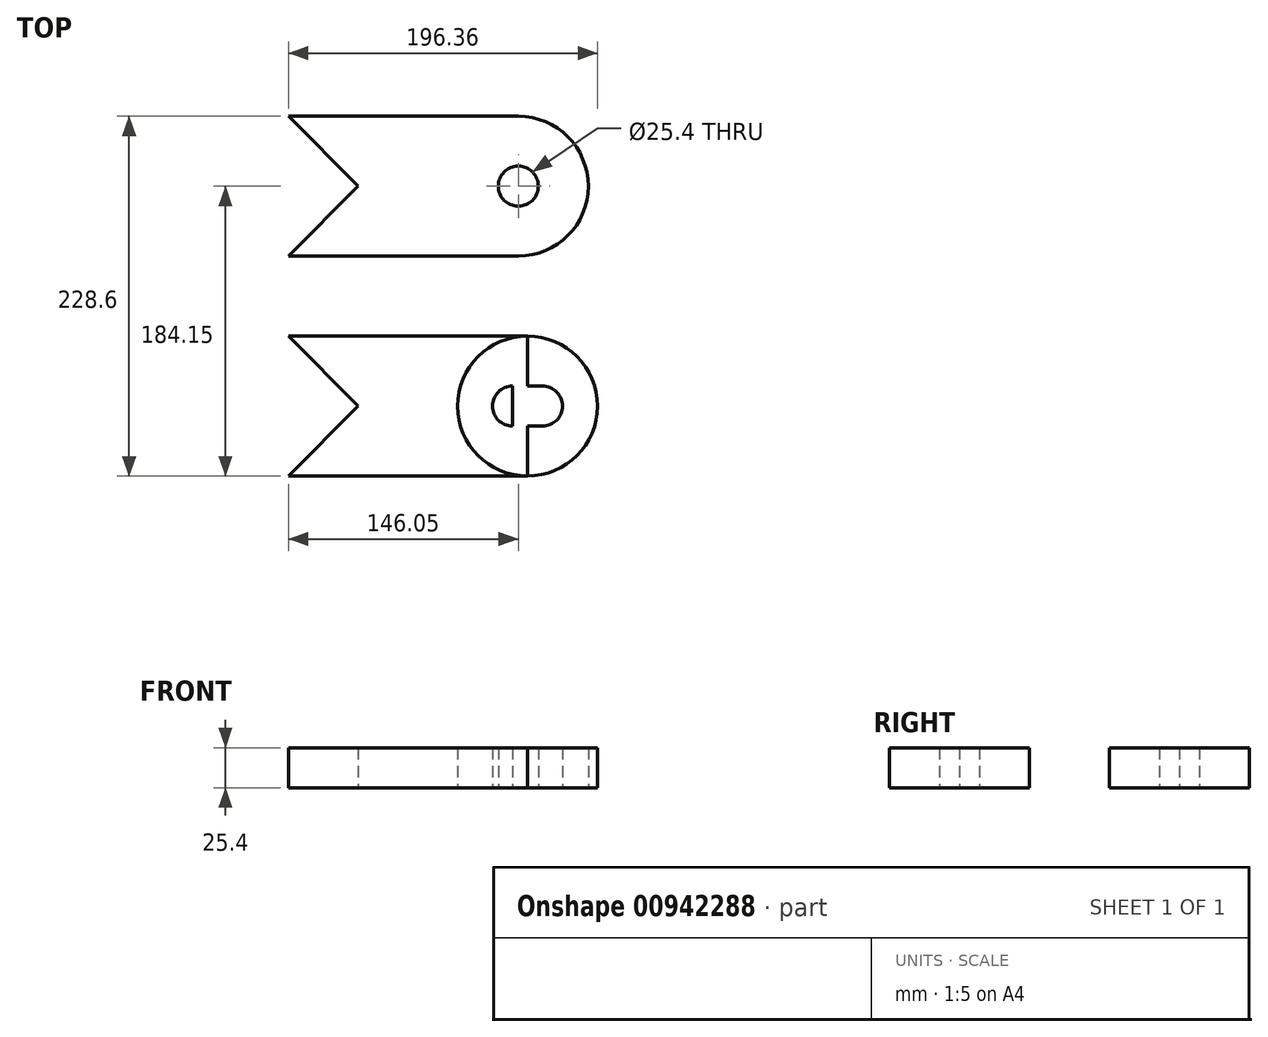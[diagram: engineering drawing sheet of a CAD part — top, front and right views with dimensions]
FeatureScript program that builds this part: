
annotation { "Feature Type Name" : "Feature", "Feature Type Description" : "" }
export const myFeature = defineFeature(function(context is Context, id is Id, definition is map)
    precondition{}
    {
        {
            var Q0;
            Q0=qCreatedBy(makeId("Top.planeOp"),FACE);
            var sketch = newSketch(context, id + "F0", { "sketchPlane" : qUnion([Q0])});
            skLineSegment(sketch, "E0.bottom", {"start": v(0, 0) * mm, "end": v(101.6, 0) * mm});
            skLineSegment(sketch, "E0.top", {"start": v(0, 88.9) * mm, "end": v(101.6, 88.9) * mm});
            skLineSegment(sketch, "E0.left", {"start": v(0, 0) * mm, "end": v(0, 88.9) * mm});
            skLineSegment(sketch, "E0.right", {"start": v(101.6, 0) * mm, "end": v(101.6, 88.9) * mm});
            skCircle(sketch, "E1", {"center": v(101.6, 44.45) * mm, "radius": 44.45 * mm});
            skLineSegment(sketch, "E2", {"start": v(0, 44.45) * mm, "end": v(-44.45, 88.9) * mm});
            skLineSegment(sketch, "E3", {"start": v(0, 44.45) * mm, "end": v(-44.45, 0) * mm});
            skLineSegment(sketch, "E4", {"start": v(0, 0) * mm, "end": v(-44.45, 0) * mm});
            skLineSegment(sketch, "E5", {"start": v(0, 88.9) * mm, "end": v(-44.45, 88.9) * mm});
            skCircle(sketch, "E6", {"center": v(101.6, 44.45) * mm, "radius": 12.7 * mm});
            skLineSegment(sketch, "E7.bottom", {"start": v(0, -50.8) * mm, "end": v(107.46, -50.8) * mm});
            skLineSegment(sketch, "E7.top", {"start": v(0, -139.7) * mm, "end": v(107.46, -139.7) * mm});
            skLineSegment(sketch, "E7.left", {"start": v(0, -50.8) * mm, "end": v(0, -139.7) * mm});
            skLineSegment(sketch, "E7.right", {"start": v(107.46, -50.8) * mm, "end": v(107.46, -139.7) * mm});
            skCircle(sketch, "E8", {"center": v(107.46, -95.25) * mm, "radius": 44.45 * mm});
            skLineSegment(sketch, "E9", {"start": v(-44.45, 0) * mm, "end": v(-44.45, -150.03) * mm});
            skLineSegment(sketch, "E10", {"start": v(0, -95.25) * mm, "end": v(-44.45, -50.8) * mm});
            skLineSegment(sketch, "E11", {"start": v(-44.45, -50.8) * mm, "end": v(0, -50.8) * mm});
            skLineSegment(sketch, "E12", {"start": v(0, -95.25) * mm, "end": v(-44.45, -139.7) * mm});
            skLineSegment(sketch, "E13", {"start": v(-44.45, -139.7) * mm, "end": v(0, -139.7) * mm});
            skArc(sketch, "E14", {"start": v(116.99, -107.95) * mm, "mid": v(129.69, -95.25) * mm, "end": v(116.99, -82.55) * mm});
            skArc(sketch, "E15.MirrorC", {"start": v(97.94, -107.95) * mm, "mid": v(85.24, -95.25) * mm, "end": v(97.94, -82.55) * mm});
            skLineSegment(sketch, "E16", {"start": v(97.94, -95.25) * mm, "end": v(97.94, -82.55) * mm});
            skLineSegment(sketch, "E17", {"start": v(97.94, -82.55) * mm, "end": v(116.99, -82.55) * mm});
            skLineSegment(sketch, "E18", {"start": v(97.94, -95.25) * mm, "end": v(97.94, -107.95) * mm});
            skLineSegment(sketch, "E19", {"start": v(97.94, -107.95) * mm, "end": v(116.99, -107.95) * mm});
            skSolve(sketch);
        }
        {
            var Q0;
            {var subQ2=sQuery(id+"F0.wireOp",EDGE,"E2");Q0=makeQuery(id+"F0.imprint","IMPRINT",FACE,{"disambiguationData":[TD([[makeQuery(id+"F0.imprint","IMPRINT",EDGE,{"derivedFrom":subQ2}),-1.0]])]});}
            var Q1;
            {var subQ2=sQuery(id+"F0.wireOp",EDGE,"E3");Q1=makeQuery(id+"F0.imprint","IMPRINT",FACE,{"disambiguationData":[TD([[makeQuery(id+"F0.imprint","IMPRINT",EDGE,{"derivedFrom":subQ2}),1.0]])]});}
            var Q2;
            {var subQ3=sQuery(id+"F0.wireOp",EDGE,"E0.bottom");Q2=makeQuery(id+"F0.imprint","IMPRINT",FACE,{"disambiguationData":[TD([[makeQuery(id+"F0.imprint","IMPRINT",EDGE,{"derivedFrom":subQ3}),1.0]])]});}
            var Q3;
            {var subQ1=sQuery(id+"F0.wireOp",EDGE,"E0.right");var subQ3=sQuery(id+"F0.wireOp",EDGE,"E6");var subQ4=makeQuery(id+"F0.imprint","INTERSECT",VERTEX,{"disambiguationData":[OD(0.0)],"derivedFrom":[subQ1,subQ3]});Q3=makeQuery(id+"F0.imprint","IMPRINT",FACE,{"disambiguationData":[TD([[makeQuery(id+"F0.imprint","IMPRINT",EDGE,{"disambiguationData":[TD([[subQ4,1.0]])],"derivedFrom":subQ3}),-1.0]])]});}
            var Q4;
            {var subQ1=sQuery(id+"F0.wireOp",EDGE,"E0.right");var subQ3=sQuery(id+"F0.wireOp",EDGE,"E6");var subQ4=makeQuery(id+"F0.imprint","INTERSECT",VERTEX,{"disambiguationData":[OD(0.0)],"derivedFrom":[subQ1,subQ3]});Q4=makeQuery(id+"F0.imprint","IMPRINT",FACE,{"disambiguationData":[TD([[makeQuery(id+"F0.imprint","IMPRINT",EDGE,{"disambiguationData":[TD([[subQ4,-1.0]])],"derivedFrom":subQ3}),-1.0]])]});}
            var Q5;
            {var subQ2=sQuery(id+"F0.wireOp",EDGE,"E10");Q5=makeQuery(id+"F0.imprint","IMPRINT",FACE,{"disambiguationData":[TD([[makeQuery(id+"F0.imprint","IMPRINT",EDGE,{"derivedFrom":subQ2}),-1.0]])]});}
            var Q6;
            {var subQ2=sQuery(id+"F0.wireOp",EDGE,"E12");Q6=makeQuery(id+"F0.imprint","IMPRINT",FACE,{"disambiguationData":[TD([[makeQuery(id+"F0.imprint","IMPRINT",EDGE,{"derivedFrom":subQ2}),1.0]])]});}
            var Q7;
            {var subQ3=sQuery(id+"F0.wireOp",EDGE,"E7.bottom");Q7=makeQuery(id+"F0.imprint","IMPRINT",FACE,{"disambiguationData":[TD([[makeQuery(id+"F0.imprint","IMPRINT",EDGE,{"derivedFrom":subQ3}),-1.0]])]});}
            var Q8;
            {var subQ0=sQuery(id+"F0.wireOp",EDGE,"E15.MirrorC");Q8=makeQuery(id+"F0.imprint","IMPRINT",FACE,{"disambiguationData":[TD([[makeQuery(id+"F0.imprint","IMPRINT",EDGE,{"derivedFrom":subQ0}),1.0]])]});}
            var Q9;
            {var subQ6=sQuery(id+"F0.wireOp",EDGE,"E14");Q9=makeQuery(id+"F0.imprint","IMPRINT",FACE,{"disambiguationData":[TD([[makeQuery(id+"F0.imprint","IMPRINT",EDGE,{"derivedFrom":subQ6}),-1.0]])]});}
            extrude(context, id + "F1", {"entities" : qUnion([Q0, Q1, Q2, Q3, Q4, Q5, Q6, Q7, Q8, Q9]), "depth" : 25.4 * mm, "offsetDistance" : 25.4 * mm});
        }
    });
